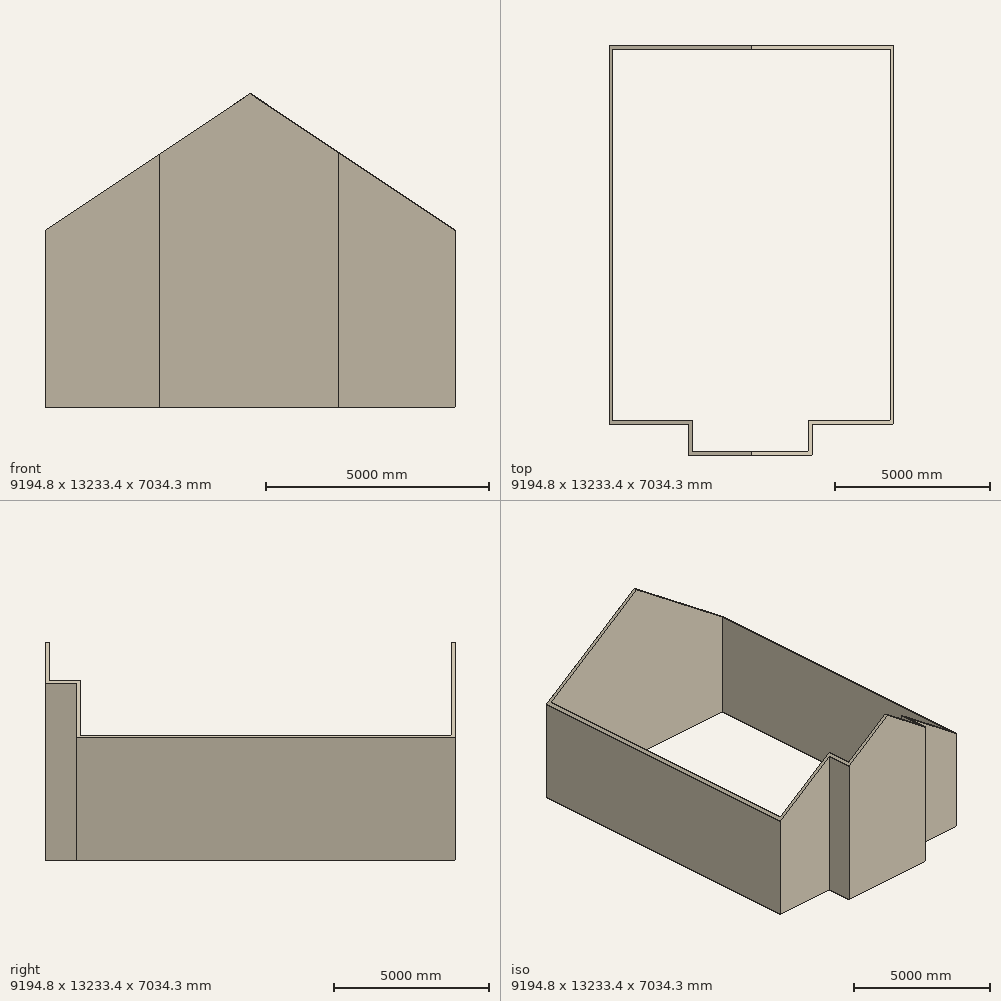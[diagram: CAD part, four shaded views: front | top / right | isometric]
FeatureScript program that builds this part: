
annotation { "Feature Type Name" : "Feature", "Feature Type Description" : "" }
export const myFeature = defineFeature(function(context is Context, id is Id, definition is map)
    precondition{}
    {
        {
            var Q0;
            Q0=qCreatedBy(makeId("Top.planeOp"),FACE);
            var sketch = newSketch(context, id + "F0", { "sketchPlane" : qUnion([Q0])});
            skLineSegment(sketch, "E0.rect.bottom", {"start": v(4495.8, 0) * mm, "end": v(1879.6, 0) * mm});
            skLineSegment(sketch, "E0.rect.top", {"start": v(4495.8, 11963.4) * mm, "end": v(-4445, 11963.4) * mm});
            skLineSegment(sketch, "E0.rect.left", {"start": v(4495.8, 0) * mm, "end": v(4495.8, 11963.4) * mm});
            skLineSegment(sketch, "E0.rect.right", {"start": v(-4445, 0) * mm, "end": v(-4445, 11963.4) * mm});
            skPoint(sketch, "E0.rect.middle", {"position": v(25.4, 5981.7) * mm});
            skLineSegment(sketch, "E1", {"start": v(0, 11963.4) * mm, "end": v(0, -1016) * mm, "construction": true});
            skLineSegment(sketch, "E2", {"start": v(-1879.6, 0) * mm, "end": v(-1879.6, -1016) * mm});
            skLineSegment(sketch, "E3", {"start": v(-1879.6, -1016) * mm, "end": v(1879.6, -1016) * mm});
            skLineSegment(sketch, "E4", {"start": v(1879.6, -1016) * mm, "end": v(1879.6, 0) * mm});
            skLineSegment(sketch, "E5.trimOffspring", {"start": v(-1879.6, 0) * mm, "end": v(-4445, 0) * mm});
            skLineSegment(sketch, "E6.0", {"start": v(4622.8, -127) * mm, "end": v(4622.8, 12090.4) * mm});
            skLineSegment(sketch, "E6.1", {"start": v(4622.8, -127) * mm, "end": v(2006.6, -127) * mm});
            skLineSegment(sketch, "E6.2", {"start": v(2006.6, -1143) * mm, "end": v(2006.6, -127) * mm});
            skLineSegment(sketch, "E6.3", {"start": v(-2006.6, -1143) * mm, "end": v(2006.6, -1143) * mm});
            skLineSegment(sketch, "E6.4", {"start": v(-2006.6, -127) * mm, "end": v(-2006.6, -1143) * mm});
            skLineSegment(sketch, "E6.5", {"start": v(4622.8, 12090.4) * mm, "end": v(-4572, 12090.4) * mm});
            skLineSegment(sketch, "E6.6", {"start": v(-2006.6, -127) * mm, "end": v(-4572, -127) * mm});
            skLineSegment(sketch, "E6.7", {"start": v(-4572, -127) * mm, "end": v(-4572, 12090.4) * mm});
            skSolve(sketch);
        }
        {
            var Q0;
            Q0 = qSketchRegion(id + "F0", true);
            extrude(context, id + "F1", {"entities" : qUnion([Q0]), "depth" : 7620 * mm});
        }
        {
            var Q0;
            Q0=makeQuery(id+"F1.opExtrude","SWEPT_FACE",FACE,{"disambiguationData":[OSD([sQuery(id+"F0.wireOp",EDGE,"E6.5")])]});
            var sketch = newSketch(context, id + "F2", { "sketchPlane" : qUnion([Q0])});
            skLineSegment(sketch, "E7", {"start": v(-4876.8, 3792.68) * mm, "end": v(-25.4, 7034.28) * mm});
            skLineSegment(sketch, "E8", {"start": v(-25.4, 7034.28) * mm, "end": v(4826, 3792.68) * mm});
            skLineSegment(sketch, "E9", {"start": v(4826, 3792.68) * mm, "end": v(4826, 7874) * mm});
            skLineSegment(sketch, "E10", {"start": v(4826, 7874) * mm, "end": v(-4876.8, 7874) * mm});
            skLineSegment(sketch, "E11", {"start": v(-4876.8, 7874) * mm, "end": v(-4876.8, 3792.68) * mm});
            skLineSegment(sketch, "E12", {"start": v(-25.4, 0) * mm, "end": v(-25.4, 7620) * mm, "construction": true});
            skPoint(sketch, "E13", {"position": v(-4622.8, 3962.4) * mm});
            skPoint(sketch, "E14", {"position": v(4572, 3962.4) * mm});
            skSolve(sketch);
        }
        {
            var Q0;
            Q0 = qSketchRegion(id + "F2", true);
            extrude(context, id + "F3", {"entities" : qUnion([Q0]), "operationType" : NewBodyOperationType.REMOVE, "endBound" : BoundingType.THROUGH_ALL, "oppositeDirection" : true, "depth" : 25.4 * mm});
        }
    });
